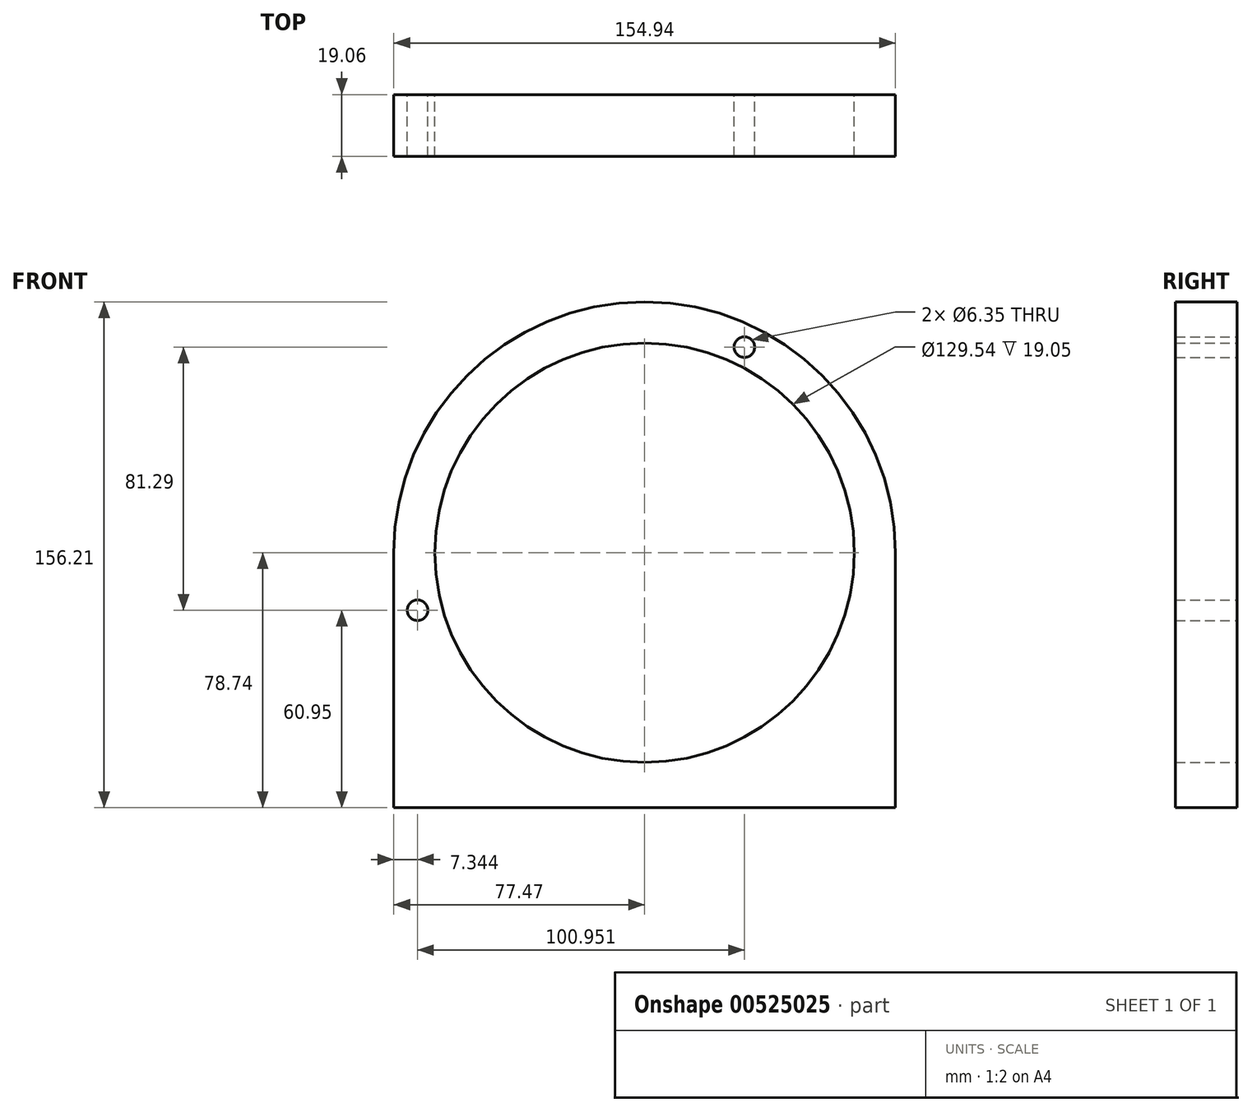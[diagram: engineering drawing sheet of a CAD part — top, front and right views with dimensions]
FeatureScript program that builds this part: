
annotation { "Feature Type Name" : "Feature", "Feature Type Description" : "" }
export const myFeature = defineFeature(function(context is Context, id is Id, definition is map)
    precondition{}
    {
        {
            var Q0;
            Q0=qCreatedBy(makeId("Front.planeOp"),FACE);
            var sketch = newSketch(context, id + "F0", { "sketchPlane" : qUnion([Q0])});
            skLineSegment(sketch, "E0", {"start": v(0, 0) * mm, "end": v(38.1, 0) * mm});
            skLineSegment(sketch, "E1", {"start": v(0, 0) * mm, "end": v(-38.1, 0) * mm});
            skLineSegment(sketch, "E2", {"start": v(0, 0) * mm, "end": v(0, -38.1) * mm});
            skLineSegment(sketch, "E3", {"start": v(0, 0) * mm, "end": v(0, 63.5) * mm});
            skLineSegment(sketch, "E4", {"start": v(0, 63.5) * mm, "end": v(0, 64.77) * mm});
            skLineSegment(sketch, "E5", {"start": v(0, -38.1) * mm, "end": v(0, -44.45) * mm});
            skFitSpline(sketch, "E6", {"points": [v(0, 63.5) * mm, v(-38.1, 0) * mm, v(0, -38.1) * mm, v(38.1, 0) * mm, v(0, 63.5) * mm]});
            skLineSegment(sketch, "E7", {"start": v(0, -44.45) * mm, "end": v(0, 64.77) * mm});
            skLineSegment(sketch, "E8", {"start": v(0, 63.5) * mm, "end": v(0, -38.1) * mm});
            skLineSegment(sketch, "E9", {"start": v(0, -38.1) * mm, "end": v(0, 12.7) * mm});
            skLineSegment(sketch, "E10", {"start": v(0, 12.7) * mm, "end": v(-50.8, 12.7) * mm});
            skLineSegment(sketch, "E11", {"start": v(0, 12.7) * mm, "end": v(50.8, 12.7) * mm});
            skCircle(sketch, "E12", {"center": v(30.83, 63.5) * mm, "radius": 3.18 * mm});
            skCircle(sketch, "E13", {"center": v(0, 0) * mm, "radius": 38.1 * mm});
            skLineSegment(sketch, "E14", {"start": v(38.1, 0) * mm, "end": v(63.5, 0) * mm});
            skLineSegment(sketch, "E15", {"start": v(-38.1, 0) * mm, "end": v(-63.5, 0) * mm});
            skLineSegment(sketch, "E16", {"start": v(0, -38.1) * mm, "end": v(0, -63.5) * mm});
            skCircle(sketch, "E17", {"center": v(0, 0) * mm, "radius": 64.77 * mm});
            skPoint(sketch, "E18.orphan", {"position": v(0, 76.2) * mm});
            skLineSegment(sketch, "E19", {"start": v(0, 64.77) * mm, "end": v(0, 77.47) * mm});
            skCircle(sketch, "E20", {"center": v(0, 0) * mm, "radius": 77.47 * mm});
            skLineSegment(sketch, "E21", {"start": v(-77.47, 0) * mm, "end": v(-77.47, -78.74) * mm});
            skLineSegment(sketch, "E22", {"start": v(-77.47, -78.74) * mm, "end": v(77.47, -78.74) * mm});
            skLineSegment(sketch, "E23", {"start": v(77.47, -78.74) * mm, "end": v(77.47, 0) * mm});
            skLineSegment(sketch, "E24", {"start": v(0, 0) * mm, "end": v(-77.47, -19.65) * mm});
            skLineSegment(sketch, "E25", {"start": v(-77.47, -19.65) * mm, "end": v(-62.78, -15.93) * mm});
            skCircle(sketch, "E26", {"center": v(-70.13, -17.8) * mm, "radius": 3.18 * mm});
            skSolve(sketch);
        }
        {
            var Q0;
            Q0 = qSketchRegion(id + "F0", true);
            extrude(context, id + "F1", {"entities" : qUnion([Q0]), "depth" : 9.52 * mm, "offsetDistance" : 25.4 * mm, "hasSecondDirection" : true, "secondDirectionOppositeDirection" : true, "secondDirectionDepth" : 9.52 * mm});
        }
    });
